# Revit family: NLRS_57_AIR_UN_door-overflow-grill-wbde_LT_sacs
name_source: partatom
category: Air Terminals
units: mm (PartAtom-declared; Revit-internal decimal feet)

## family parameters
Always vertical = Yes
Cut with Voids When Loaded = No
OmniClass Number = 23.75.70.21.27.11
OmniClass Title = Diffusers, Registers, and Grilles
Part Type = Normal
Room Calculation Point = No
Round Connector Dimension = Use Diameter
Shared = No
Work Plane-Based = No

## types (1)
- WDBE
    Assembly Code = 57.00
    Cost = 0 $
    Default Elevation = 0 mm  [stored 0 ft]
    Description = Firerated wall/door overflow grill, Type WDBE
    IfcDescription = Firerated wall/door overflow grill, Type WDBE
    IfcExportAs = IfcAirterminal
    IfcExportType = Diffuser
    Manufacturer = Solid Air Climate Solutions
    Max Flow = 0 m³/h
    Min Flow = 0 m³/h
    Model = WDBE
    NLRS_C_content_datum_uitgifte = 01-04-2024
    NLRS_C_content_provider = Solid Air Climate Solutions
    NLRS_C_content_versie = 2.21.01
    NLRS_C_description = Firerated wall/door overflow grill, Type WDBE
    SACS_Data_Hidden = WDBE
    SACS_Dummy = 1
    Type Comments = See documentation for EN 13501-2 classification
    URL = https://solid-air.nl

note: [stored X ft] marks values corroborated as IEEE doubles in the binary element streams (Revit-internal decimal feet)

## geometry (parser evidence)
native form markers: Sweep x14
no freeform markers — native parametric forms only
